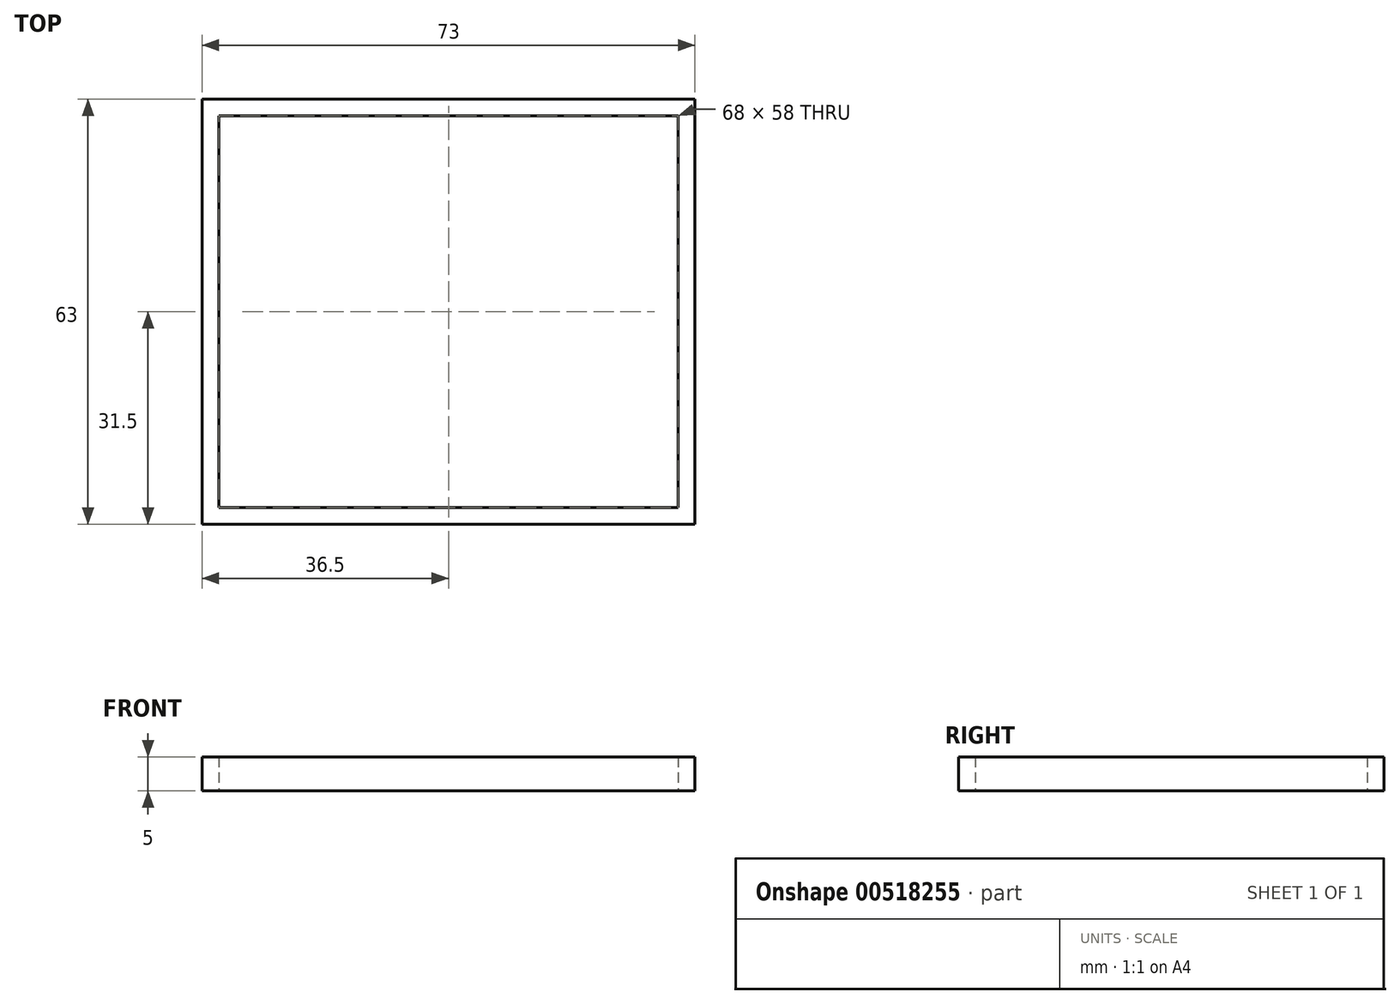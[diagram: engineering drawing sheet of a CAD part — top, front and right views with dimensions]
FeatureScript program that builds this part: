
annotation { "Feature Type Name" : "Feature", "Feature Type Description" : "" }
export const myFeature = defineFeature(function(context is Context, id is Id, definition is map)
    precondition{}
    {
        {
            var Q0;
            Q0=qCreatedBy(makeId("Top.planeOp"),FACE);
            var sketch = newSketch(context, id + "F0", { "sketchPlane" : qUnion([Q0])});
            skLineSegment(sketch, "E0.bottom", {"start": v(34, 29) * mm, "end": v(-34, 29) * mm});
            skLineSegment(sketch, "E0.top", {"start": v(34, -29) * mm, "end": v(-34, -29) * mm});
            skLineSegment(sketch, "E0.left", {"start": v(34, 29) * mm, "end": v(34, -29) * mm});
            skLineSegment(sketch, "E0.right", {"start": v(-34, 29) * mm, "end": v(-34, -29) * mm});
            skPoint(sketch, "E0.middle", {"position": v(0, 0) * mm});
            skLineSegment(sketch, "E1.bottom", {"start": v(-36.5, 31.5) * mm, "end": v(36.5, 31.5) * mm});
            skLineSegment(sketch, "E1.top", {"start": v(-36.5, -31.5) * mm, "end": v(36.5, -31.5) * mm});
            skLineSegment(sketch, "E1.left", {"start": v(-36.5, 31.5) * mm, "end": v(-36.5, -31.5) * mm});
            skLineSegment(sketch, "E1.right", {"start": v(36.5, 31.5) * mm, "end": v(36.5, -31.5) * mm});
            skSolve(sketch);
        }
        {
            var Q0;
            Q0=makeQuery(id+"F0.imprint","IMPRINT",FACE,{"disambiguationData":[TD([[makeQuery(id+"F0.imprint","IMPRINT",EDGE,{"derivedFrom":sQuery(id+"F0.wireOp",EDGE,"E0.bottom")}),-1.0]])]});
            extrude(context, id + "F1", {"entities" : qUnion([Q0]), "depth" : 5 * mm, "offsetDistance" : 25 * mm});
        }
    });
